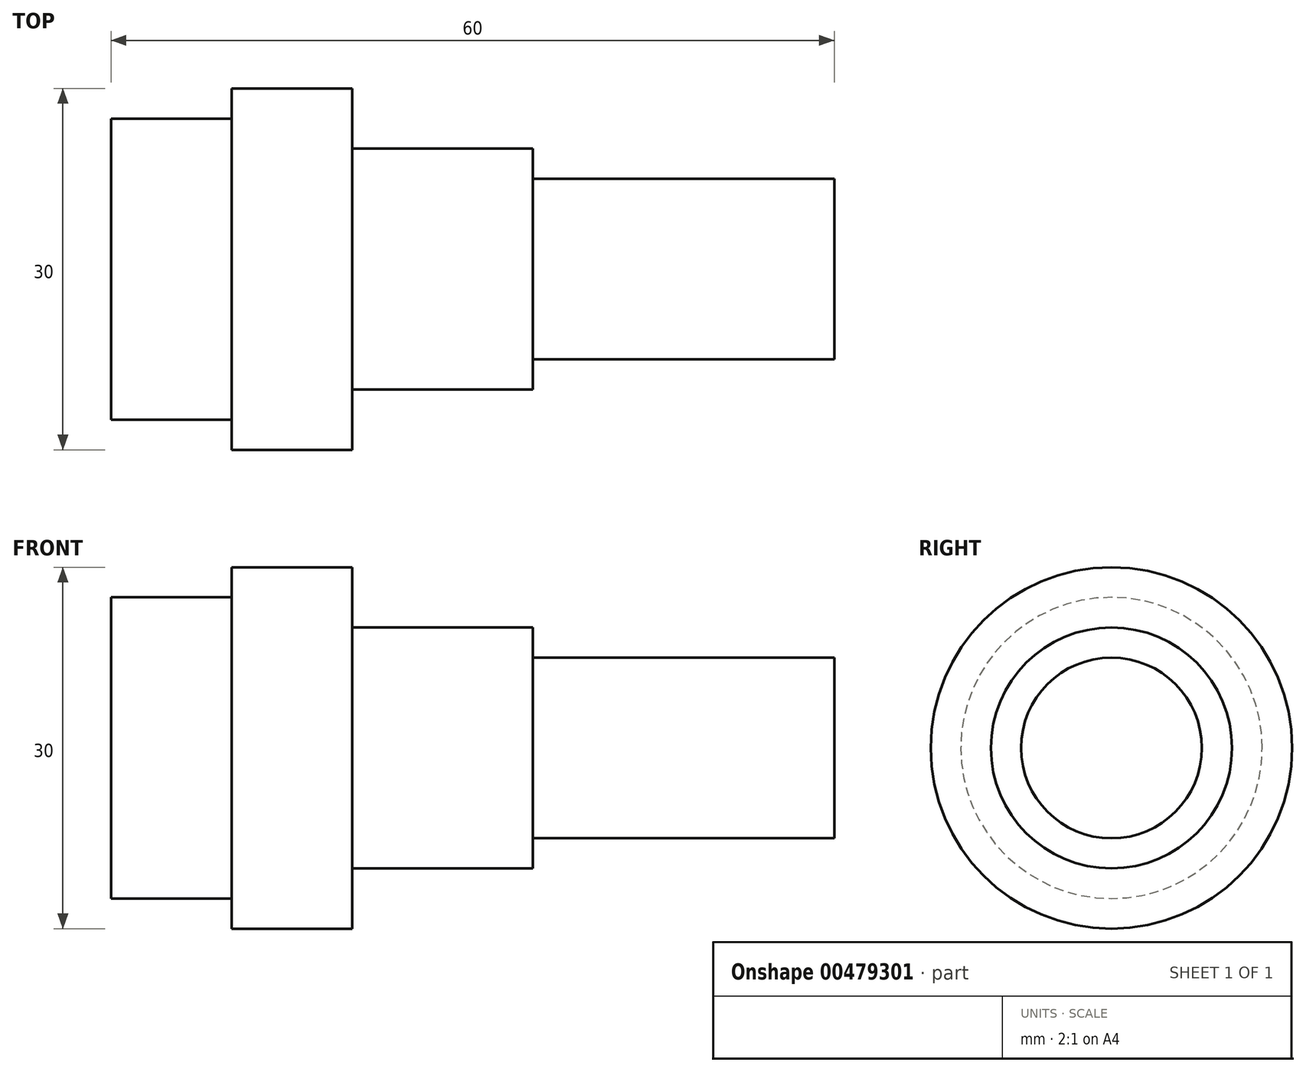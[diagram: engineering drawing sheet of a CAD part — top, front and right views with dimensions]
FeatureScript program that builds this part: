
annotation { "Feature Type Name" : "Feature", "Feature Type Description" : "" }
export const myFeature = defineFeature(function(context is Context, id is Id, definition is map)
    precondition{}
    {
        {
            var Q0;
            Q0=qCreatedBy(makeId("Right.planeOp"),FACE);
            var sketch = newSketch(context, id + "F0", { "sketchPlane" : qUnion([Q0])});
            skCircle(sketch, "E0", {"center": v(0, 0) * mm, "radius": 15 * mm});
            skSolve(sketch);
        }
        {
            var Q0;
            Q0 = qSketchRegion(id + "F0", true);
            extrude(context, id + "F1", {"entities" : qUnion([Q0]), "depth" : 10 * mm});
        }
        {
            var Q0;
            Q0=makeQuery(id+"F1.opExtrude","CAP_FACE",FACE,{"disambiguationData":[OSD([sQuery(id+"F0.wireOp",EDGE,"E0")])],"isStart":false});
            var sketch = newSketch(context, id + "F2", { "sketchPlane" : qUnion([Q0])});
            skCircle(sketch, "E1", {"center": v(0, 0) * mm, "radius": 10 * mm});
            skSolve(sketch);
        }
        {
            var Q0;
            Q0 = qSketchRegion(id + "F2", true);
            extrude(context, id + "F3", {"entities" : qUnion([Q0]), "operationType" : NewBodyOperationType.ADD, "depth" : 15 * mm});
        }
        {
            var Q0;
            Q0=makeQuery(id+"F3.opExtrude","CAP_FACE",FACE,{"disambiguationData":[OSD([sQuery(id+"F2.wireOp",EDGE,"E1")])],"isStart":false});
            var sketch = newSketch(context, id + "F4", { "sketchPlane" : qUnion([Q0])});
            skCircle(sketch, "E2", {"center": v(0, 0) * mm, "radius": 7.5 * mm});
            skSolve(sketch);
        }
        {
            var Q0;
            Q0 = qSketchRegion(id + "F4", true);
            extrude(context, id + "F5", {"entities" : qUnion([Q0]), "operationType" : NewBodyOperationType.ADD, "depth" : 25 * mm});
        }
        {
            var Q0;
            Q0=makeQuery(id+"F1.opExtrude","CAP_FACE",FACE,{"disambiguationData":[OSD([sQuery(id+"F0.wireOp",EDGE,"E0")])],"isStart":true});
            var sketch = newSketch(context, id + "F6", { "sketchPlane" : qUnion([Q0])});
            skCircle(sketch, "E3", {"center": v(0, 0) * mm, "radius": 12.5 * mm});
            skSolve(sketch);
        }
        {
            var Q0;
            Q0 = qSketchRegion(id + "F6", true);
            extrude(context, id + "F7", {"entities" : qUnion([Q0]), "operationType" : NewBodyOperationType.ADD, "depth" : 10 * mm});
        }
    });
